# Revit family: hAmmereinsatz Typ 2520 für Staberder ST, BP und OMEX
name_source: partatom
category: Generic Models
revit_build: Autodesk Revit 2015 (Build: 20140606_1530(x64)
units: mm (PartAtom-declared; Revit-internal decimal feet)

## types (2) — shared parameters
Height = 200 mm  [stored 0.656168 ft]
Height 2 = 20 mm  [stored 0.0656168 ft]
Height 3 = 120 mm  [stored 0.393701 ft]
Height 4 = 25 mm  [stored 0.082021 ft]
Length = 34 mm
Manufacturer = OBO Bettermann
Material = Steel
URL = http://www.obo-bettermann.com
Width = 20 mm  [stored 0.0656168 ft]
Width 2 = 14 mm  [stored 0.0459318 ft]

## per-type parameters (varying)
| type | GTIN | Height 1 | Manufacturer Art.No. | Width 1 |
| 2520 20 | 4012195243793 | 47 mm  [stored 0.154199 ft] | 3043703 | 7 mm  [stored 0.0229659 ft] |
| 2520 25 | 4012195243854 | 52 mm | 3043754 | 8 mm  [stored 0.0262467 ft] |

note: column(s) folded — value = type name in every type: Article Type

note: [stored X ft] marks values corroborated as IEEE doubles in the binary element streams (Revit-internal decimal feet)

## geometry (parser evidence)
native form markers: Sweep x2
no freeform markers — native parametric forms only
